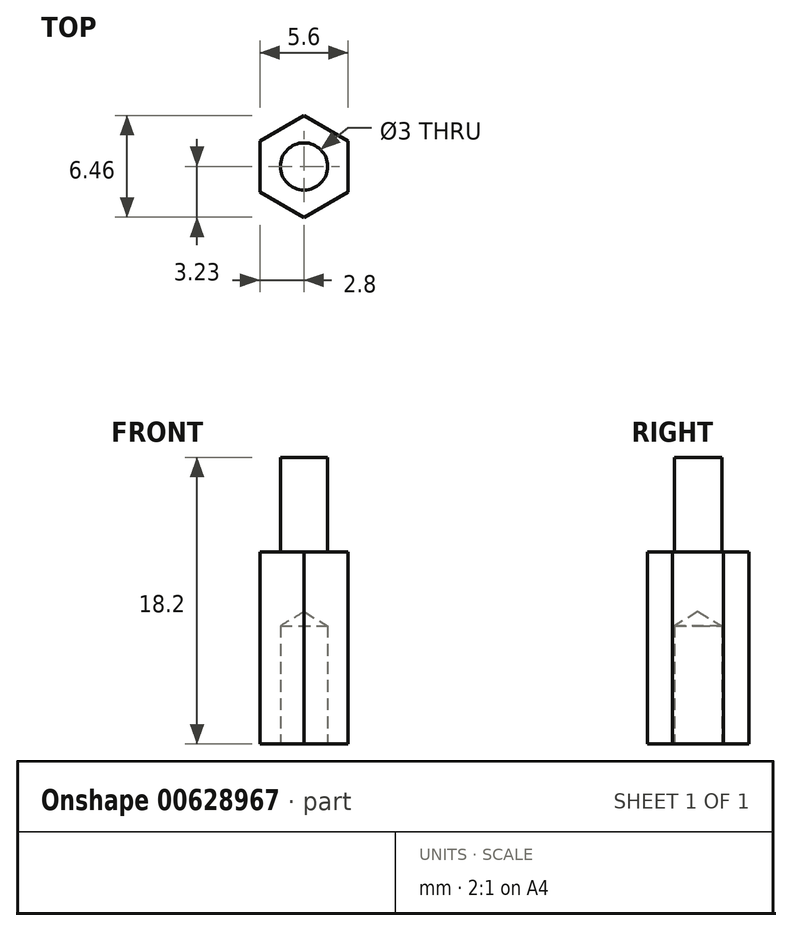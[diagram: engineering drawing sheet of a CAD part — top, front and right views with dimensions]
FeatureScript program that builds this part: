
annotation { "Feature Type Name" : "Feature", "Feature Type Description" : "" }
export const myFeature = defineFeature(function(context is Context, id is Id, definition is map)
    precondition{}
    {
        {
            var Q0;
            Q0=qCreatedBy(makeId("Top.planeOp"),FACE);
            var sketch = newSketch(context, id + "F0", { "sketchPlane" : qUnion([Q0])});
            skCircle(sketch, "E0.cCircle", {"center": v(0, 0) * mm, "radius": 2.8 * mm, "construction": true});
            skLineSegment(sketch, "E0.0", {"start": v(2.8, 1.62) * mm, "end": v(2.8, -1.62) * mm});
            skLineSegment(sketch, "E0.1", {"start": v(2.8, -1.62) * mm, "end": v(0, -3.23) * mm});
            skLineSegment(sketch, "E0.2", {"start": v(0, -3.23) * mm, "end": v(-2.8, -1.62) * mm});
            skLineSegment(sketch, "E0.3", {"start": v(-2.8, -1.62) * mm, "end": v(-2.8, 1.62) * mm});
            skLineSegment(sketch, "E0.4", {"start": v(-2.8, 1.62) * mm, "end": v(0, 3.23) * mm});
            skLineSegment(sketch, "E0.5", {"start": v(0, 3.23) * mm, "end": v(2.8, 1.62) * mm});
            skPoint(sketch, "E0.0.midPoint", {"position": v(2.8, 0) * mm});
            skSolve(sketch);
        }
        {
            var Q0;
            Q0=makeQuery(id+"F0.imprint","IMPRINT",FACE,{"disambiguationData":[TD([[makeQuery(id+"F0.imprint","IMPRINT",EDGE,{"derivedFrom":sQuery(id+"F0.wireOp",EDGE,"E0.0")}),-1.0]])]});
            extrude(context, id + "F1", {"entities" : qUnion([Q0]), "depth" : 12.2 * mm, "offsetDistance" : 25 * mm});
        }
        {
            var Q0;
            Q0=sQuery(id+"F0.wireOp",VERTEX,"E0.cCircle.center");
            var Q1;
            Q1=makeQuery(id+"F1.opExtrude","SWEPT_BODY",BODY,{"disambiguationData":[OSD([sQuery(id+"F0.wireOp",EDGE,"E0.0"),sQuery(id+"F0.wireOp",EDGE,"E0.1"),sQuery(id+"F0.wireOp",EDGE,"E0.2"),sQuery(id+"F0.wireOp",EDGE,"E0.3"),sQuery(id+"F0.wireOp",EDGE,"E0.4"),sQuery(id+"F0.wireOp",EDGE,"E0.5")])]});
            hole(context, id + "F2", {"style" : HoleStyle.SIMPLE, "endStyle" : HoleEndStyle.BLIND, "oppositeDirection" : true, "holeDiameter" : 3 * mm, "majorDiameter" : 5 * mm, "holeDepth" : 7.5 * mm, "isTappedThrough" : true, "tappedDepth" : 2.3 * mm, "tapClearance" : 3, "startFromSketch" : true, "locations" : qUnion([Q0]), "scope" : qUnion([Q1])});
        }
        {
            var Q0;
            Q0=makeQuery(id+"F1.opExtrude","CAP_FACE",FACE,{"disambiguationData":[OSD([sQuery(id+"F0.wireOp",EDGE,"E0.0"),sQuery(id+"F0.wireOp",EDGE,"E0.1"),sQuery(id+"F0.wireOp",EDGE,"E0.2"),sQuery(id+"F0.wireOp",EDGE,"E0.3"),sQuery(id+"F0.wireOp",EDGE,"E0.4"),sQuery(id+"F0.wireOp",EDGE,"E0.5")])],"isStart":false});
            var sketch = newSketch(context, id + "F3", { "sketchPlane" : qUnion([Q0])});
            skCircle(sketch, "E1", {"center": v(0, 0) * mm, "radius": 1.5 * mm});
            skSolve(sketch);
        }
        {
            var Q0;
            Q0=makeQuery(id+"F3.imprint","IMPRINT",FACE,{"disambiguationData":[TD([[makeQuery(id+"F3.imprint","IMPRINT",EDGE,{"derivedFrom":sQuery(id+"F3.wireOp",EDGE,"E1")}),1.0]])]});
            extrude(context, id + "F4", {"entities" : qUnion([Q0]), "operationType" : NewBodyOperationType.ADD, "depth" : 6 * mm, "offsetDistance" : 25 * mm});
        }
    });
